annotation { "Feature Type Name" : "Feature", "Feature Type Description" : "" }
export const myFeature = defineFeature(function(context is Context, id is Id, definition is map)
    precondition{}
    {
        {
            var Q0;
            Q0=qCreatedBy(makeId("Top.planeOp"),FACE);
            var sketch = newSketch(context, id + "F0", { "sketchPlane" : qUnion([Q0])});
            skLineSegment(sketch, "E0.bottom", {"start": v(96.48, 55.38) * mm, "end": v(-96.48, 55.38) * mm});
            skLineSegment(sketch, "E0.top", {"start": v(96.48, -55.38) * mm, "end": v(-96.48, -55.38) * mm});
            skLineSegment(sketch, "E0.left", {"start": v(96.48, 55.38) * mm, "end": v(96.48, -55.38) * mm});
            skLineSegment(sketch, "E0.right", {"start": v(-96.48, 55.38) * mm, "end": v(-96.48, -55.38) * mm});
            skPoint(sketch, "E0.middle", {"position": v(0, 0) * mm});
            skLineSegment(sketch, "E1.bottom", {"start": v(77, 44.37) * mm, "end": v(-77, 44.37) * mm});
            skLineSegment(sketch, "E1.top", {"start": v(77, -42.35) * mm, "end": v(-77, -42.35) * mm});
            skLineSegment(sketch, "E1.left", {"start": v(77, 44.37) * mm, "end": v(77, -42.35) * mm});
            skLineSegment(sketch, "E1.right", {"start": v(-77, 44.37) * mm, "end": v(-77, -42.35) * mm});
            skPoint(sketch, "E1.middle", {"position": v(0, 1.01) * mm});
            skLineSegment(sketch, "E2", {"start": v(0, -42.35) * mm, "end": v(0, -55.38) * mm, "construction": true});
            skLineSegment(sketch, "E3.bottom", {"start": v(39.98, 35.92) * mm, "end": v(-27.02, 35.92) * mm});
            skLineSegment(sketch, "E3.top", {"start": v(39.98, -49.08) * mm, "end": v(-27.02, -49.08) * mm});
            skLineSegment(sketch, "E3.left", {"start": v(39.98, 35.92) * mm, "end": v(39.98, -49.08) * mm});
            skLineSegment(sketch, "E3.right", {"start": v(-27.02, 35.92) * mm, "end": v(-27.02, -49.08) * mm});
            skLineSegment(sketch, "E4", {"start": v(17.98, -49.08) * mm, "end": v(17.98, -53.08) * mm});
            skLineSegment(sketch, "E5", {"start": v(17.98, -53.08) * mm, "end": v(-27.02, -53.08) * mm});
            skLineSegment(sketch, "E6", {"start": v(-27.02, -53.08) * mm, "end": v(-27.02, -49.08) * mm});
            skCircle(sketch, "E7", {"center": v(-63.1, 33.8) * mm, "radius": 1.5 * mm});
            skCircle(sketch, "E8", {"center": v(-63.1, -31.85) * mm, "radius": 1.5 * mm});
            skCircle(sketch, "E9.MirrorC", {"center": v(63.1, -31.85) * mm, "radius": 1.5 * mm});
            skCircle(sketch, "E10.MirrorC", {"center": v(63.1, 33.8) * mm, "radius": 1.5 * mm});
            skLineSegment(sketch, "E11", {"start": v(96.48, 55.38) * mm, "end": v(-96.48, -55.38) * mm, "construction": true});
            skSolve(sketch);
        }
        {
            var Q0;
            Q0=makeQuery(id+"F0.imprint","IMPRINT",FACE,{"disambiguationData":[TD([[makeQuery(id+"F0.imprint","IMPRINT",EDGE,{"derivedFrom":sQuery(id+"F0.wireOp",EDGE,"E0.bottom")}),1.0]])]});
            var Q1;
            Q1=makeQuery(id+"F0.imprint","IMPRINT",FACE,{"disambiguationData":[TD([[makeQuery(id+"F0.imprint","IMPRINT",EDGE,{"derivedFrom":sQuery(id+"F0.wireOp",EDGE,"E1.bottom")}),1.0]])]});
            var Q2;
            {var subQ5=sQuery(id+"F0.wireOp",EDGE,"E3.bottom");Q2=makeQuery(id+"F0.imprint","IMPRINT",FACE,{"disambiguationData":[TD([[makeQuery(id+"F0.imprint","IMPRINT",EDGE,{"derivedFrom":subQ5}),1.0]])]});}
            var Q3;
            {var subQ2=sQuery(id+"F0.wireOp",EDGE,"E4");Q3=makeQuery(id+"F0.imprint","IMPRINT",FACE,{"disambiguationData":[TD([[makeQuery(id+"F0.imprint","IMPRINT",EDGE,{"derivedFrom":subQ2}),-1.0]])]});}
            var Q4;
            {var subQ0=sQuery(id+"F0.wireOp",EDGE,"E3.left");var subQ3=sQuery(id+"F0.wireOp",EDGE,"E1.top");var subQ4=makeQuery(id+"F0.imprint","INTERSECT",VERTEX,{"derivedFrom":[subQ3,subQ0]});Q4=makeQuery(id+"F0.imprint","IMPRINT",FACE,{"disambiguationData":[TD([[makeQuery(id+"F0.imprint","IMPRINT",EDGE,{"disambiguationData":[TD([[subQ4,-1.0]])],"derivedFrom":subQ3}),1.0]])]});}
            var Q5;
            Q5=makeQuery(id+"F0.imprint","IMPRINT",FACE,{"disambiguationData":[TD([[makeQuery(id+"F0.imprint","IMPRINT",EDGE,{"derivedFrom":sQuery(id+"F0.wireOp",EDGE,"E10.MirrorC")}),-1.0]])]});
            var Q6;
            Q6=makeQuery(id+"F0.imprint","IMPRINT",FACE,{"disambiguationData":[TD([[makeQuery(id+"F0.imprint","IMPRINT",EDGE,{"derivedFrom":sQuery(id+"F0.wireOp",EDGE,"E9.MirrorC")}),-1.0]])]});
            var Q7;
            Q7=makeQuery(id+"F0.imprint","IMPRINT",FACE,{"disambiguationData":[TD([[makeQuery(id+"F0.imprint","IMPRINT",EDGE,{"derivedFrom":sQuery(id+"F0.wireOp",EDGE,"E8")}),1.0]])]});
            var Q8;
            Q8=makeQuery(id+"F0.imprint","IMPRINT",FACE,{"disambiguationData":[TD([[makeQuery(id+"F0.imprint","IMPRINT",EDGE,{"derivedFrom":sQuery(id+"F0.wireOp",EDGE,"E7")}),1.0]])]});
            extrude(context, id + "F1", {"entities" : qUnion([Q0, Q1, Q2, Q3, Q4, Q5, Q6, Q7, Q8]), "depth" : 9.7 * mm});
        }
        {
            var Q0;
            Q0=makeQuery(id+"F1.opExtrude","SWEPT_EDGE",EDGE,{"disambiguationData":[OSD([sQuery(id+"F0.wireOp",EDGE,"E0.top"),sQuery(id+"F0.wireOp",EDGE,"E0.right")])]});
            var Q1;
            Q1=makeQuery(id+"F1.opExtrude","SWEPT_EDGE",EDGE,{"disambiguationData":[OSD([sQuery(id+"F0.wireOp",EDGE,"E0.top"),sQuery(id+"F0.wireOp",EDGE,"E0.left")])]});
            var Q2;
            Q2=makeQuery(id+"F1.opExtrude","SWEPT_EDGE",EDGE,{"disambiguationData":[OSD([sQuery(id+"F0.wireOp",EDGE,"E0.bottom"),sQuery(id+"F0.wireOp",EDGE,"E0.left")])]});
            var Q3;
            Q3=makeQuery(id+"F1.opExtrude","SWEPT_EDGE",EDGE,{"disambiguationData":[OSD([sQuery(id+"F0.wireOp",EDGE,"E0.bottom"),sQuery(id+"F0.wireOp",EDGE,"E0.right")])]});
            fillet(context, id + "F2", {"entities" : qUnion([Q0, Q1, Q2, Q3]), "radius" : 7.5 * mm, "tangentPropagation" : true, "allowEdgeOverflow" : false});
        }
        {
            var Q0;
            Q0=makeQuery(id+"F1.opExtrude","CAP_FACE",FACE,{"disambiguationData":[OSD([sQuery(id+"F0.wireOp",EDGE,"E0.bottom"),sQuery(id+"F0.wireOp",EDGE,"E0.top"),sQuery(id+"F0.wireOp",EDGE,"E0.left"),sQuery(id+"F0.wireOp",EDGE,"E0.right")])],"isStart":false});
            var sketch = newSketch(context, id + "F3", { "sketchPlane" : qUnion([Q0])});
            skLineSegment(sketch, "E12.0", {"start": v(-77, 44.37) * mm, "end": v(-77, -42.35) * mm});
            skLineSegment(sketch, "E12.1", {"start": v(77, -42.35) * mm, "end": v(-77, -42.35) * mm});
            skLineSegment(sketch, "E12.2", {"start": v(77, 44.37) * mm, "end": v(-77, 44.37) * mm});
            skLineSegment(sketch, "E12.3", {"start": v(77, 44.37) * mm, "end": v(77, -42.35) * mm});
            skSolve(sketch);
        }
        {
            var Q0;
            Q0 = qSketchRegion(id + "F3", true);
            extrude(context, id + "F4", {"entities" : qUnion([Q0]), "operationType" : NewBodyOperationType.REMOVE, "oppositeDirection" : true, "depth" : .2 * mm});
        }
        {
            var Q0;
            {var subQ5=sQuery(id+"F0.wireOp",EDGE,"E3.bottom");Q0=makeQuery(id+"F0.imprint","IMPRINT",FACE,{"disambiguationData":[TD([[makeQuery(id+"F0.imprint","IMPRINT",EDGE,{"derivedFrom":subQ5}),1.0]])]});}
            var Q1;
            {var subQ0=sQuery(id+"F0.wireOp",EDGE,"E3.left");var subQ3=sQuery(id+"F0.wireOp",EDGE,"E1.top");var subQ4=makeQuery(id+"F0.imprint","INTERSECT",VERTEX,{"derivedFrom":[subQ3,subQ0]});Q1=makeQuery(id+"F0.imprint","IMPRINT",FACE,{"disambiguationData":[TD([[makeQuery(id+"F0.imprint","IMPRINT",EDGE,{"disambiguationData":[TD([[subQ4,-1.0]])],"derivedFrom":subQ3}),1.0]])]});}
            var Q2;
            {var subQ2=sQuery(id+"F0.wireOp",EDGE,"E4");Q2=makeQuery(id+"F0.imprint","IMPRINT",FACE,{"disambiguationData":[TD([[makeQuery(id+"F0.imprint","IMPRINT",EDGE,{"derivedFrom":subQ2}),-1.0]])]});}
            extrude(context, id + "F5", {"entities" : qUnion([Q0, Q1, Q2]), "operationType" : NewBodyOperationType.REMOVE, "depth" : 3.3 * mm});
        }
        {
            var Q0;
            Q0=qCreatedBy(makeId("Top.planeOp"),FACE);
            var sketch = newSketch(context, id + "F6", { "sketchPlane" : qUnion([Q0])});
            skLineSegment(sketch, "E13.bottom", {"start": v(-26.02, 32.42) * mm, "end": v(38.98, 32.42) * mm});
            skLineSegment(sketch, "E13.top", {"start": v(-26.02, -23.58) * mm, "end": v(38.98, -23.58) * mm});
            skLineSegment(sketch, "E13.left", {"start": v(-26.02, 32.42) * mm, "end": v(-26.02, -23.58) * mm});
            skLineSegment(sketch, "E13.right", {"start": v(38.98, 32.42) * mm, "end": v(38.98, -23.58) * mm});
            skPoint(sketch, "E13.middle", {"position": v(6.48, 4.42) * mm});
            skLineSegment(sketch, "E14", {"start": v(6.48, 4.42) * mm, "end": v(6.48, 35.92) * mm, "construction": true});
            skSolve(sketch);
        }
        {
            var Q0;
            Q0 = qSketchRegion(id + "F6", true);
            extrude(context, id + "F7", {"entities" : qUnion([Q0]), "endBound" : BoundingType.SYMMETRIC, "depth" : 1.6 * mm});
        }
        {
            var Q0;
            Q0=makeQuery(id+"F7.opExtrude","SWEPT_EDGE",EDGE,{"disambiguationData":[OSD([sQuery(id+"F6.wireOp",EDGE,"E13.top"),sQuery(id+"F6.wireOp",EDGE,"E13.right")])]});
            var Q1;
            Q1=makeQuery(id+"F7.opExtrude","SWEPT_EDGE",EDGE,{"disambiguationData":[OSD([sQuery(id+"F6.wireOp",EDGE,"E13.top"),sQuery(id+"F6.wireOp",EDGE,"E13.left")])]});
            var Q2;
            Q2=makeQuery(id+"F7.opExtrude","SWEPT_EDGE",EDGE,{"disambiguationData":[OSD([sQuery(id+"F6.wireOp",EDGE,"E13.bottom"),sQuery(id+"F6.wireOp",EDGE,"E13.left")])]});
            var Q3;
            Q3=makeQuery(id+"F7.opExtrude","SWEPT_EDGE",EDGE,{"disambiguationData":[OSD([sQuery(id+"F6.wireOp",EDGE,"E13.bottom"),sQuery(id+"F6.wireOp",EDGE,"E13.right")])]});
            fillet(context, id + "F8", {"entities" : qUnion([Q0, Q1, Q2, Q3]), "radius" : 3 * mm, "tangentPropagation" : true, "allowEdgeOverflow" : false});
        }
        {
            var Q0;
            Q0=makeQuery(id+"F7.opExtrude","CAP_FACE",FACE,{"disambiguationData":[OSD([sQuery(id+"F6.wireOp",EDGE,"E13.bottom"),sQuery(id+"F6.wireOp",EDGE,"E13.top"),sQuery(id+"F6.wireOp",EDGE,"E13.left"),sQuery(id+"F6.wireOp",EDGE,"E13.right")])],"isStart":true});
            var sketch = newSketch(context, id + "F9", { "sketchPlane" : qUnion([Q0])});
            skLineSegment(sketch, "E15.bottom", {"start": v(-14.02, 3.28) * mm, "end": v(-28.02, 3.28) * mm});
            skLineSegment(sketch, "E15.top", {"start": v(-14.02, 16.28) * mm, "end": v(-28.02, 16.28) * mm});
            skLineSegment(sketch, "E15.left", {"start": v(-14.02, 3.28) * mm, "end": v(-14.02, 16.28) * mm});
            skLineSegment(sketch, "E15.right", {"start": v(-28.02, 3.28) * mm, "end": v(-28.02, 16.28) * mm});
            skLineSegment(sketch, "E16.bottom", {"start": v(32.38, 19.38) * mm, "end": v(24.88, 19.38) * mm});
            skLineSegment(sketch, "E16.top", {"start": v(32.38, 25.08) * mm, "end": v(24.88, 25.08) * mm});
            skLineSegment(sketch, "E16.left", {"start": v(32.38, 19.38) * mm, "end": v(32.38, 25.08) * mm});
            skLineSegment(sketch, "E16.right", {"start": v(24.88, 19.38) * mm, "end": v(24.88, 25.08) * mm});
            skLineSegment(sketch, "E17.bottom", {"start": v(38.98, -17) * mm, "end": v(32.98, -17) * mm});
            skLineSegment(sketch, "E17.top", {"start": v(38.98, 4) * mm, "end": v(32.98, 4) * mm});
            skLineSegment(sketch, "E17.left", {"start": v(38.98, -17) * mm, "end": v(38.98, 4) * mm});
            skLineSegment(sketch, "E17.right", {"start": v(32.98, -17) * mm, "end": v(32.98, 4) * mm});
            skLineSegment(sketch, "E18", {"start": v(38.98, -6.5) * mm, "end": v(32.98, -6.5) * mm, "construction": true});
            skSolve(sketch);
        }
        {
            var Q0;
            Q0=makeQuery(id+"F9.imprint","IMPRINT",FACE,{"disambiguationData":[TD([[makeQuery(id+"F9.imprint","IMPRINT",EDGE,{"derivedFrom":sQuery(id+"F9.wireOp",EDGE,"E17.bottom")}),-1.0]])]});
            extrude(context, id + "F10", {"entities" : qUnion([Q0]), "operationType" : NewBodyOperationType.ADD, "depth" : 2.8 * mm});
        }
        {
            var Q0;
            {var subQ0=sQuery(id+"F9.wireOp",EDGE,"E16.bottom");Q0=makeQuery(id+"F9.imprint","IMPRINT",FACE,{"disambiguationData":[TD([[makeQuery(id+"F9.imprint","IMPRINT",EDGE,{"derivedFrom":subQ0}),-1.0]])]});}
            var Q1;
            {var subQ0=sQuery(id+"F9.wireOp",EDGE,"E16.top");Q1=makeQuery(id+"F9.imprint","IMPRINT",FACE,{"disambiguationData":[TD([[makeQuery(id+"F9.imprint","IMPRINT",EDGE,{"derivedFrom":subQ0}),1.0]])]});}
            extrude(context, id + "F11", {"entities" : qUnion([Q0, Q1]), "operationType" : NewBodyOperationType.ADD, "depth" : 3 * mm});
        }
        {
            var Q0;
            {var subQ0=sQuery(id+"F9.wireOp",EDGE,"E15.left");Q0=makeQuery(id+"F9.imprint","IMPRINT",FACE,{"disambiguationData":[TD([[makeQuery(id+"F9.imprint","IMPRINT",EDGE,{"derivedFrom":subQ0}),1.0]])]});}
            var Q1;
            {var subQ0=sQuery(id+"F9.wireOp",EDGE,"E15.right");Q1=makeQuery(id+"F9.imprint","IMPRINT",FACE,{"disambiguationData":[TD([[makeQuery(id+"F9.imprint","IMPRINT",EDGE,{"derivedFrom":subQ0}),-1.0]])]});}
            extrude(context, id + "F12", {"entities" : qUnion([Q0, Q1]), "operationType" : NewBodyOperationType.ADD, "depth" : 6.8 * mm});
        }
        {
            var Q0;
            {var subQ8=sQuery(id+"F9.wireOp",EDGE,"E15.left");Q0=makeQuery(id+"F9.imprint","IMPRINT",FACE,{"disambiguationData":[TD([[makeQuery(id+"F9.imprint","IMPRINT",EDGE,{"derivedFrom":subQ8}),-1.0]])]});}
            var sketch = newSketch(context, id + "F13", { "sketchPlane" : qUnion([Q0])});
            skCircle(sketch, "E19", {"center": v(35.98, -29.42) * mm, "radius": 1 * mm});
            skCircle(sketch, "E20", {"center": v(35.98, 20.58) * mm, "radius": 1 * mm});
            skCircle(sketch, "E21", {"center": v(-23.02, 20.58) * mm, "radius": 1 * mm});
            skCircle(sketch, "E22", {"center": v(-23.02, -29.42) * mm, "radius": 1 * mm});
            skSolve(sketch);
        }
        {
            var Q0;
            Q0 = qSketchRegion(id + "F13", true);
            extrude(context, id + "F14", {"entities" : qUnion([Q0]), "operationType" : NewBodyOperationType.REMOVE, "oppositeDirection" : true, "depth" : 3 * mm});
        }
        {
            var Q0;
            Q0=makeQuery(id+"F0.imprint","IMPRINT",FACE,{"disambiguationData":[TD([[makeQuery(id+"F0.imprint","IMPRINT",EDGE,{"derivedFrom":sQuery(id+"F0.wireOp",EDGE,"E10.MirrorC")}),-1.0]])]});
            var Q1;
            Q1=makeQuery(id+"F0.imprint","IMPRINT",FACE,{"disambiguationData":[TD([[makeQuery(id+"F0.imprint","IMPRINT",EDGE,{"derivedFrom":sQuery(id+"F0.wireOp",EDGE,"E9.MirrorC")}),-1.0]])]});
            var Q2;
            Q2=makeQuery(id+"F0.imprint","IMPRINT",FACE,{"disambiguationData":[TD([[makeQuery(id+"F0.imprint","IMPRINT",EDGE,{"derivedFrom":sQuery(id+"F0.wireOp",EDGE,"E7")}),1.0]])]});
            var Q3;
            Q3=makeQuery(id+"F0.imprint","IMPRINT",FACE,{"disambiguationData":[TD([[makeQuery(id+"F0.imprint","IMPRINT",EDGE,{"derivedFrom":sQuery(id+"F0.wireOp",EDGE,"E8")}),1.0]])]});
            extrude(context, id + "F15", {"entities" : qUnion([Q0, Q1, Q2, Q3]), "operationType" : NewBodyOperationType.REMOVE, "depth" : 5 * mm});
        }
        {
            var Q0;
            {var subQ8=sQuery(id+"F9.wireOp",EDGE,"E15.left");Q0=makeQuery(id+"F9.imprint","IMPRINT",FACE,{"disambiguationData":[TD([[makeQuery(id+"F9.imprint","IMPRINT",EDGE,{"derivedFrom":subQ8}),-1.0]])]});}
            var sketch = newSketch(context, id + "F16", { "sketchPlane" : qUnion([Q0])});
            skCircle(sketch, "E23", {"center": v(0, 0) * mm, "radius": 6.06 * mm});
            skSolve(sketch);
        }
        {
            var Q0;
            Q0 = qSketchRegion(id + "F16", true);
            extrude(context, id + "F17", {"entities" : qUnion([Q0]), "operationType" : NewBodyOperationType.REMOVE, "oppositeDirection" : true, "depth" : 1 * mm});
        }
        {
            var Q0;
            Q0=makeQuery(id+"F10.opExtrude","CAP_FACE",FACE,{"disambiguationData":[OSD([sQuery(id+"F9.wireOp",EDGE,"E17.bottom"),sQuery(id+"F9.wireOp",EDGE,"E17.top"),sQuery(id+"F9.wireOp",EDGE,"E17.left"),sQuery(id+"F9.wireOp",EDGE,"E17.right")])],"isStart":false});
            var sketch = newSketch(context, id + "F18", { "sketchPlane" : qUnion([Q0])});
            skLineSegment(sketch, "E24.bottom", {"start": v(38.98, -14.5) * mm, "end": v(72.98, -14.5) * mm});
            skLineSegment(sketch, "E24.top", {"start": v(38.98, 1.5) * mm, "end": v(72.98, 1.5) * mm});
            skLineSegment(sketch, "E24.left", {"start": v(38.98, -14.5) * mm, "end": v(38.98, 1.5) * mm});
            skLineSegment(sketch, "E25", {"start": v(32.98, -6.5) * mm, "end": v(38.98, -6.5) * mm, "construction": true});
            skLineSegment(sketch, "E26", {"start": v(88.98, -65.5) * mm, "end": v(165.12, -65.5) * mm});
            skLineSegment(sketch, "E27", {"start": v(165.12, -65.5) * mm, "end": v(165.12, -81.5) * mm});
            skLineSegment(sketch, "E28", {"start": v(165.12, -81.5) * mm, "end": v(88.98, -81.5) * mm});
            skLineSegment(sketch, "E29", {"start": v(72.98, -65.5) * mm, "end": v(72.98, -14.5) * mm});
            skLineSegment(sketch, "E30", {"start": v(88.98, -14.5) * mm, "end": v(88.98, -65.5) * mm});
            skLineSegment(sketch, "E31", {"start": v(88.98, -65.5) * mm, "end": v(72.98, -65.5) * mm, "construction": true});
            skLineSegment(sketch, "E32", {"start": v(72.98, 1.5) * mm, "end": v(88.98, -14.5) * mm});
            skLineSegment(sketch, "E33", {"start": v(88.98, -14.5) * mm, "end": v(72.98, -14.5) * mm, "construction": true});
            skLineSegment(sketch, "E34", {"start": v(72.98, 1.5) * mm, "end": v(72.98, -14.5) * mm, "construction": true});
            skLineSegment(sketch, "E35", {"start": v(72.98, -65.5) * mm, "end": v(88.98, -81.5) * mm});
            skLineSegment(sketch, "E36", {"start": v(88.98, -65.5) * mm, "end": v(88.98, -81.5) * mm, "construction": true});
            skLineSegment(sketch, "E37", {"start": v(165.12, -73.5) * mm, "end": v(88.98, -73.5) * mm, "construction": true});
            skSolve(sketch);
        }
        {
            var Q0;
            Q0 = qSketchRegion(id + "F18", true);
            extrude(context, id + "F19", {"entities" : qUnion([Q0]), "oppositeDirection" : true, "depth" : .5 * mm});
        }
        {
            var Q0;
            Q0=makeQuery(id+"F4.boolean.opBoolean","COPY",FACE,{"derivedFrom":makeQuery(id+"F4.opExtrude","CAP_FACE",FACE,{"disambiguationData":[OSD([sQuery(id+"F3.wireOp",EDGE,"E12.0"),sQuery(id+"F3.wireOp",EDGE,"E12.1"),sQuery(id+"F3.wireOp",EDGE,"E12.2"),sQuery(id+"F3.wireOp",EDGE,"E12.3")])],"isStart":false})});
            var sketch = newSketch(context, id + "F20", { "sketchPlane" : qUnion([Q0])});
            skText(sketch, "E38", { "text": "LCD SCREEN", "fontName": "OpenSans-Bold.ttf"});
            const initialGuessF20  = {"E38": [0.02428, -0.00127, -1, 0, 0.005]};
            skSetInitialGuess(sketch, initialGuessF20);
            skSolve(sketch);
        }
        {
            var Q0;
            Q0 = qSketchRegion(id + "F20", true);
            extrude(context, id + "F21", {"entities" : qUnion([Q0]), "operationType" : NewBodyOperationType.REMOVE, "oppositeDirection" : true, "depth" : 1 * mm});
        }
        {
            var Q0;
            Q0=makeQuery(id+"F11.opExtrude","SWEPT_EDGE",EDGE,{"disambiguationData":[OSD([sQuery(id+"F9.wireOp",EDGE,"E16.top"),sQuery(id+"F9.wireOp",EDGE,"E16.right")])]});
            cPoint(context, id + "F22", {"entities" : qUnion([Q0]), "parameter" : 0.5});
        }
        {
            var Q0;
            Q0=qCreatedBy(makeId("Top.planeOp"),FACE);
            var Q1;
            Q1 = qCreatedBy(id + "F22" ,VERTEX);
            cPlane(context, id + "F23", {"entities" : qUnion([Q0, Q1]), "cplaneType" : CPlaneType.PLANE_POINT, "offset" : 25 * mm, "width" : 150 * mm, "height" : 150 * mm});
        }
        {
            var Q0;
            Q0=qCreatedBy(id+"F23.planeOp",FACE);
            var sketch = newSketch(context, id + "F24", { "sketchPlane" : qUnion([Q0])});
            skLineSegment(sketch, "E39.bottom", {"start": v(33.93, -40.08) * mm, "end": v(28.63, -40.08) * mm, "construction": true});
            skLineSegment(sketch, "E39.top", {"start": v(33.93, -28.08) * mm, "end": v(28.63, -28.08) * mm});
            skLineSegment(sketch, "E39.left", {"start": v(33.93, -40.08) * mm, "end": v(33.93, -28.08) * mm});
            skLineSegment(sketch, "E40", {"start": v(28.63, -28.08) * mm, "end": v(28.63, -55.08) * mm, "construction": true});
            skPoint(sketch, "E40.endSnap0", {"position": v(28.63, -40.08) * mm});
            skLineSegment(sketch, "E41", {"start": v(28.63, -55.08) * mm, "end": v(31.63, -55.08) * mm});
            skLineSegment(sketch, "E42", {"start": v(31.63, -55.08) * mm, "end": v(33.93, -40.08) * mm});
            skLineSegment(sketch, "E43", {"start": v(28.63, -28.08) * mm, "end": v(28.63, -25.08) * mm, "construction": true});
            skLineSegment(sketch, "E44.MirrorCS", {"start": v(25.63, -55.08) * mm, "end": v(23.33, -40.08) * mm});
            skLineSegment(sketch, "E45.MirrorCS", {"start": v(23.33, -40.08) * mm, "end": v(23.33, -28.08) * mm});
            skLineSegment(sketch, "E46.MirrorCS", {"start": v(23.33, -28.08) * mm, "end": v(28.63, -28.08) * mm});
            skLineSegment(sketch, "E47.MirrorCS", {"start": v(28.63, -55.08) * mm, "end": v(25.63, -55.08) * mm});
            skSolve(sketch);
        }
        {
            var Q0;
            Q0 = qSketchRegion(id + "F24", true);
            extrude(context, id + "F25", {"entities" : qUnion([Q0]), "endBound" : BoundingType.SYMMETRIC, "depth" : 7.6 * mm});
        }
        {
            var Q0;
            Q0=makeQuery(id+"F25.opExtrude","CAP_EDGE",EDGE,{"disambiguationData":[OSD([sQuery(id+"F24.wireOp",EDGE,"E44.MirrorCS")])],"isStart":true});
            var Q1;
            Q1=makeQuery(id+"F25.opExtrude","CAP_EDGE",EDGE,{"disambiguationData":[OSD([sQuery(id+"F24.wireOp",EDGE,"E45.MirrorCS")])],"isStart":true});
            var Q2;
            Q2=makeQuery(id+"F25.opExtrude","CAP_EDGE",EDGE,{"disambiguationData":[OSD([sQuery(id+"F24.wireOp",EDGE,"E44.MirrorCS")])],"isStart":false});
            var Q3;
            Q3=makeQuery(id+"F25.opExtrude","CAP_EDGE",EDGE,{"disambiguationData":[OSD([sQuery(id+"F24.wireOp",EDGE,"E45.MirrorCS")])],"isStart":false});
            var Q4;
            Q4=makeQuery(id+"F25.opExtrude","CAP_EDGE",EDGE,{"disambiguationData":[OSD([sQuery(id+"F24.wireOp",EDGE,"E42")])],"isStart":true});
            var Q5;
            Q5=makeQuery(id+"F25.opExtrude","CAP_EDGE",EDGE,{"disambiguationData":[OSD([sQuery(id+"F24.wireOp",EDGE,"E39.left")])],"isStart":true});
            var Q6;
            Q6=makeQuery(id+"F25.opExtrude","CAP_EDGE",EDGE,{"disambiguationData":[OSD([sQuery(id+"F24.wireOp",EDGE,"E39.left")])],"isStart":false});
            var Q7;
            Q7=makeQuery(id+"F25.opExtrude","CAP_EDGE",EDGE,{"disambiguationData":[OSD([sQuery(id+"F24.wireOp",EDGE,"E42")])],"isStart":false});
            fillet(context, id + "F26", {"entities" : qUnion([Q0, Q1, Q2, Q3, Q4, Q5, Q6, Q7]), "radius" : 2 * mm, "tangentPropagation" : true, "allowEdgeOverflow" : false});
        }
        {
            var Q0;
            Q0=makeQuery(id+"F25.opExtrude","SWEPT_FACE",FACE,{"disambiguationData":[OSD([sQuery(id+"F24.wireOp",EDGE,"E41"),sQuery(id+"F24.wireOp",EDGE,"E47.MirrorCS")])]});
            var sketch = newSketch(context, id + "F27", { "sketchPlane" : qUnion([Q0])});
            skLineSegment(sketch, "E48", {"start": v(25.63, -2.3) * mm, "end": v(31.63, -2.3) * mm});
            skCircle(sketch, "E49", {"center": v(28.63, -2.3) * mm, "radius": 1.75 * mm});
            skSolve(sketch);
        }
        {
            var Q0;
            Q0 = qSketchRegion(id + "F27", true);
            extrude(context, id + "F28", {"entities" : qUnion([Q0]), "operationType" : NewBodyOperationType.ADD, "depth" : 50 * mm});
        }
        {
            var Q0;
            Q0=makeQuery(id+"F25.opExtrude","SWEPT_FACE",FACE,{"disambiguationData":[OSD([sQuery(id+"F24.wireOp",EDGE,"E39.top"),sQuery(id+"F24.wireOp",EDGE,"E46.MirrorCS")])]});
            var sketch = newSketch(context, id + "F29", { "sketchPlane" : qUnion([Q0])});
            skLineSegment(sketch, "E50.bottom", {"start": v(-31.73, -3.54) * mm, "end": v(-25.53, -3.54) * mm});
            skLineSegment(sketch, "E50.top", {"start": v(-31.73, -1.06) * mm, "end": v(-25.53, -1.06) * mm});
            skLineSegment(sketch, "E50.left", {"start": v(-31.73, -3.54) * mm, "end": v(-31.73, -1.06) * mm});
            skLineSegment(sketch, "E50.right", {"start": v(-25.53, -3.54) * mm, "end": v(-25.53, -1.06) * mm});
            skPoint(sketch, "E50.middle", {"position": v(-28.63, -2.3) * mm});
            skLineSegment(sketch, "E51", {"start": v(-28.63, -6.1) * mm, "end": v(-28.63, 1.5) * mm, "construction": true});
            skSolve(sketch);
        }
        {
            var Q0;
            Q0=makeQuery(id+"F29.imprint","IMPRINT",FACE,{"disambiguationData":[TD([[makeQuery(id+"F29.imprint","IMPRINT",EDGE,{"derivedFrom":sQuery(id+"F29.wireOp",EDGE,"E50.bottom")}),1.0]])]});
            extrude(context, id + "F30", {"entities" : qUnion([Q0]), "operationType" : NewBodyOperationType.ADD, "depth" : 8 * mm});
        }
    });